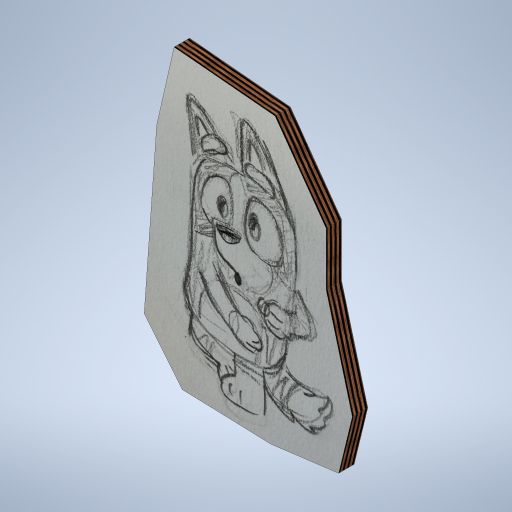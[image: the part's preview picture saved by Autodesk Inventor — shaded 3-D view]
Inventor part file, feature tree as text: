
AUTODESK INVENTOR PART (.ipt)
format: ipt  version: 2023 (Build 270158000, 158)  size: 1,350,144 bytes
history: native  units: in
note: dims shown in document units (in); Inventor stores cm internally (conversion verified against a paired STEP export)
features: extrude x1, sketch x1, other x1
ambient origin geometry x8: Origin, YZ Plane, XZ Plane, XY Plane, X Axis, Y Axis, Z Axis, Center Point
bodies: Solid1 (feature_tree)
feature tree (3):
  extrude  "Extrusion1"  Depth=1.0in
  sketch  "Sketch1"  dims[d5=1.0in d6=0.0in d7=13.4415in d10=19.0899in]
  other  "Image1"
